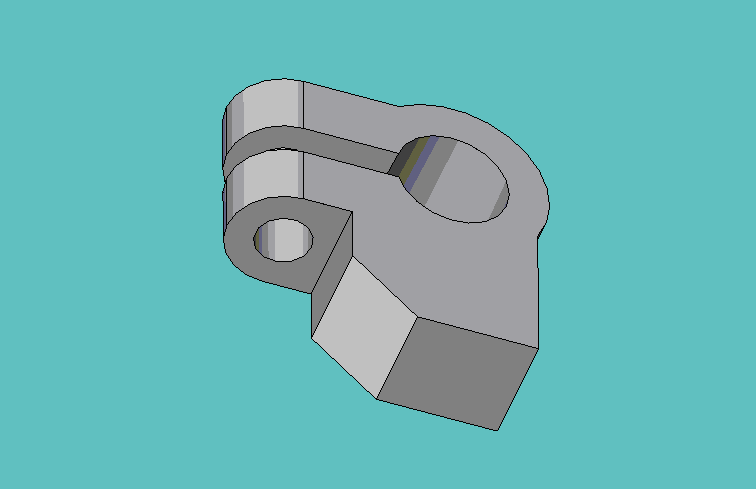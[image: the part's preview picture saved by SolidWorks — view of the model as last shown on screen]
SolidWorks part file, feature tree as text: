
SOLIDWORKS PART (.sldprt)
format: sldprt  version: not decoded by parser v0  size: 273,920 bytes
history: native  units: mm
features: sketch x9, cut_extrude x4, plane x3, hole x2, material x1, extrude x1, fillet x1 (+7 scaffold rows collapsed)
feature tree (28):
  scaffold x7  (default folders/planes/origin — collapsed)
  material  "Matériau <non spécifié>"
  plane  "Face"
  plane  "Dessus"
  plane  "Droite"
  sketch  "Esquisse1"  dims[c1.D3=48.0mm c1.D1=20.0mm c1.D2=51.0mm c1.D4=50.0mm c1.D5=26.0mm c1.D6=30.0mm c1.D7=15.0mm c1.D8=72.0mm c1.D9=20.0mm c2.D1=20.0mm]
  extrude  "Base-Extrusion"  Depth=28mm
  sketch  "Esquisse2"  dims[D1=~5.085706mm]
  cut_extrude  "Enlèv. mat.-Extru.1"  [1 undecoded]
  fillet  "Congé2"  Radius=14mm
  sketch  "Esquisse3"  dims[D1=14.0mm]
  cut_extrude  "Enlèv. mat.-Extru.2"  [1 undecoded]
  sketch  "Esquisse4"  dims[D1=12.0mm D2=14.0mm D3=14.0mm]
  cut_extrude  "Enlèv. mat.-Extru.3"  Depth=20mm
  sketch  "Esquisse7"  dims[D1=8.0mm D2=16.0mm]
  cut_extrude  "Enlèv. mat.-Extru.5"  [1 undecoded]
  hole  "Dégagement M1.62"  Diameter=12mm Depth=12mm
  sketch  "Esquisse14"
  sketch  "Esquisse13"  dims[hole-wizard template sketch: 46 standard entries collapsed; hole parameters kept: c15.Diamètre du perçage=12.0mm c15.Profondeur du perçage=12.0mm c15.D3=~14.816244mm c15.Angle de pointe=118.0deg]
  hole  "Dégagement M1.63"  Diameter=12mm Depth=24mm
  sketch  "Esquisse18"  dims[D1=14.0mm D2=14.0mm]
  sketch  "Esquisse17"  dims[hole-wizard template sketch: 46 standard entries collapsed; hole parameters kept: c15.Diamètre du perçage=12.0mm c15.Profondeur du perçage=24.0mm c15.D3=~14.816244mm c15.Angle de pointe=120.0deg]
decode coverage: 13 of 17 modeling features carry decoded parameters
note: ~ marks probable driven/reference dimensions
note: 3 parameter values undecoded
summary: no parameter record found for 3 features
note: suppression state not decoded; provenance and decode notes live in map.json
